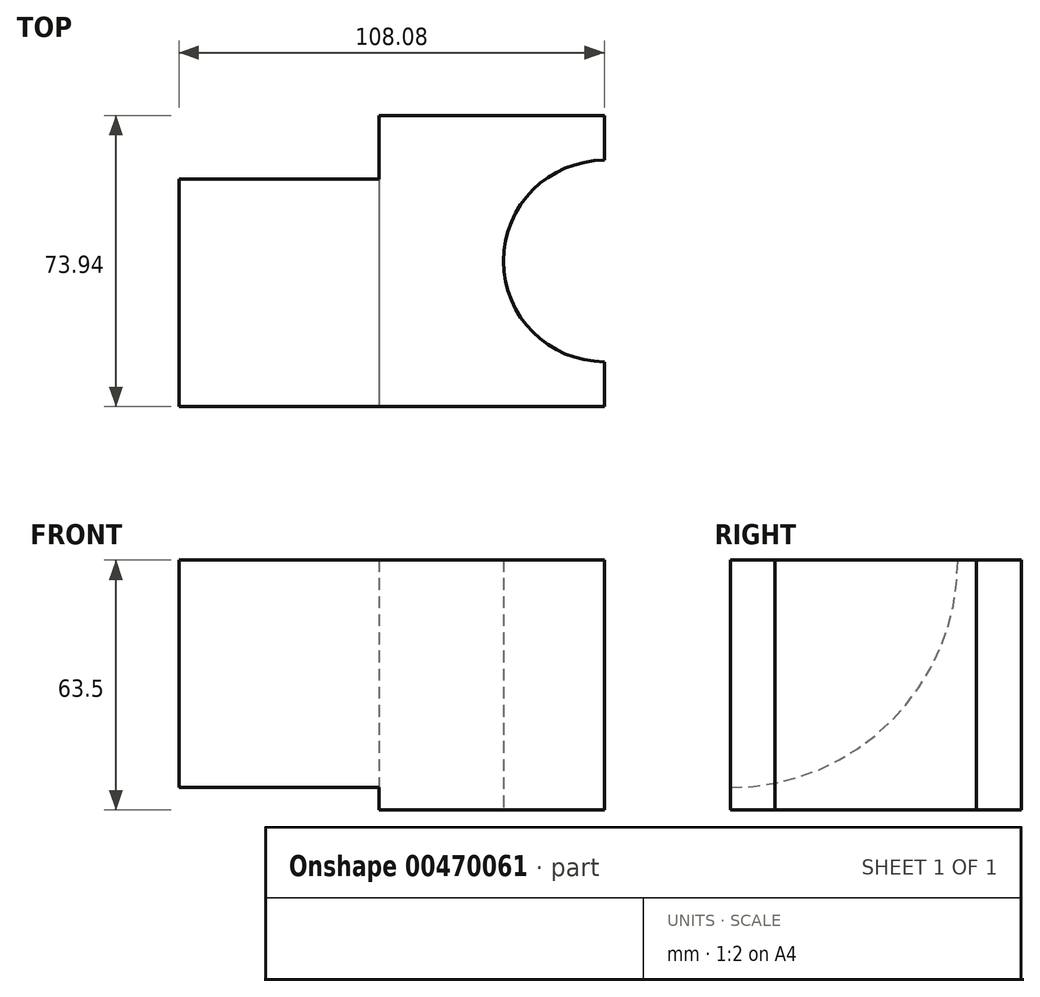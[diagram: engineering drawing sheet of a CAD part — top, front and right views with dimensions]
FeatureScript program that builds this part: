
annotation { "Feature Type Name" : "Feature", "Feature Type Description" : "" }
export const myFeature = defineFeature(function(context is Context, id is Id, definition is map)
    precondition{}
    {
        {
            var Q0;
            Q0=qCreatedBy(makeId("Top.planeOp"),FACE);
            var sketch = newSketch(context, id + "F0", { "sketchPlane" : qUnion([Q0])});
            skLineSegment(sketch, "E0.bottom", {"start": v(54.04, 36.97) * mm, "end": v(-54.04, 36.97) * mm});
            skLineSegment(sketch, "E0.top", {"start": v(54.04, -36.97) * mm, "end": v(-54.04, -36.97) * mm});
            skLineSegment(sketch, "E0.left", {"start": v(54.04, 36.97) * mm, "end": v(54.04, 25.6) * mm});
            skLineSegment(sketch, "E0.right", {"start": v(-54.04, 36.97) * mm, "end": v(-54.04, -36.97) * mm});
            skPoint(sketch, "E0.middle", {"position": v(0, 0) * mm});
            skArc(sketch, "E1", {"start": v(54.04, -25.6) * mm, "mid": v(28.44, 0) * mm, "end": v(54.04, 25.6) * mm});
            skLineSegment(sketch, "E2.trimOffspring", {"start": v(54.04, -25.6) * mm, "end": v(54.04, -36.97) * mm});
            skSolve(sketch);
        }
        {
            var Q0;
            Q0 = qSketchRegion(id + "F0", true);
            extrude(context, id + "F1", {"entities" : qUnion([Q0]), "depth" : 63.5 * mm});
        }
        {
            var Q0;
            Q0=makeQuery(id+"F1.opExtrude","SWEPT_FACE",FACE,{"disambiguationData":[OSD([sQuery(id+"F0.wireOp",EDGE,"E0.right")])]});
            var sketch = newSketch(context, id + "F2", { "sketchPlane" : qUnion([Q0])});
            skArc(sketch, "E3", {"start": v(36.97, 5.69) * mm, "mid": v(-3.9, 22.62) * mm, "end": v(-20.84, 63.5) * mm});
            skLineSegment(sketch, "E4", {"start": v(-20.84, 63.5) * mm, "end": v(36.97, 63.5) * mm});
            skSolve(sketch);
        }
        {
            var Q0;
            Q0 = qSketchRegion(id + "F2", true);
            var Q1;
            {var subQ0=sQuery(id+"F2.wireOp",EDGE,"E3");Q1=makeQuery(id+"F2.imprint","IMPRINT",FACE,{"disambiguationData":[TD([[makeQuery(id+"F2.imprint","IMPRINT",EDGE,{"derivedFrom":subQ0}),-1.0]])]});}
            extrude(context, id + "F3", {"entities" : qUnion([Q0, Q1]), "operationType" : NewBodyOperationType.REMOVE, "oppositeDirection" : true, "depth" : 50.8 * mm});
        }
    });
